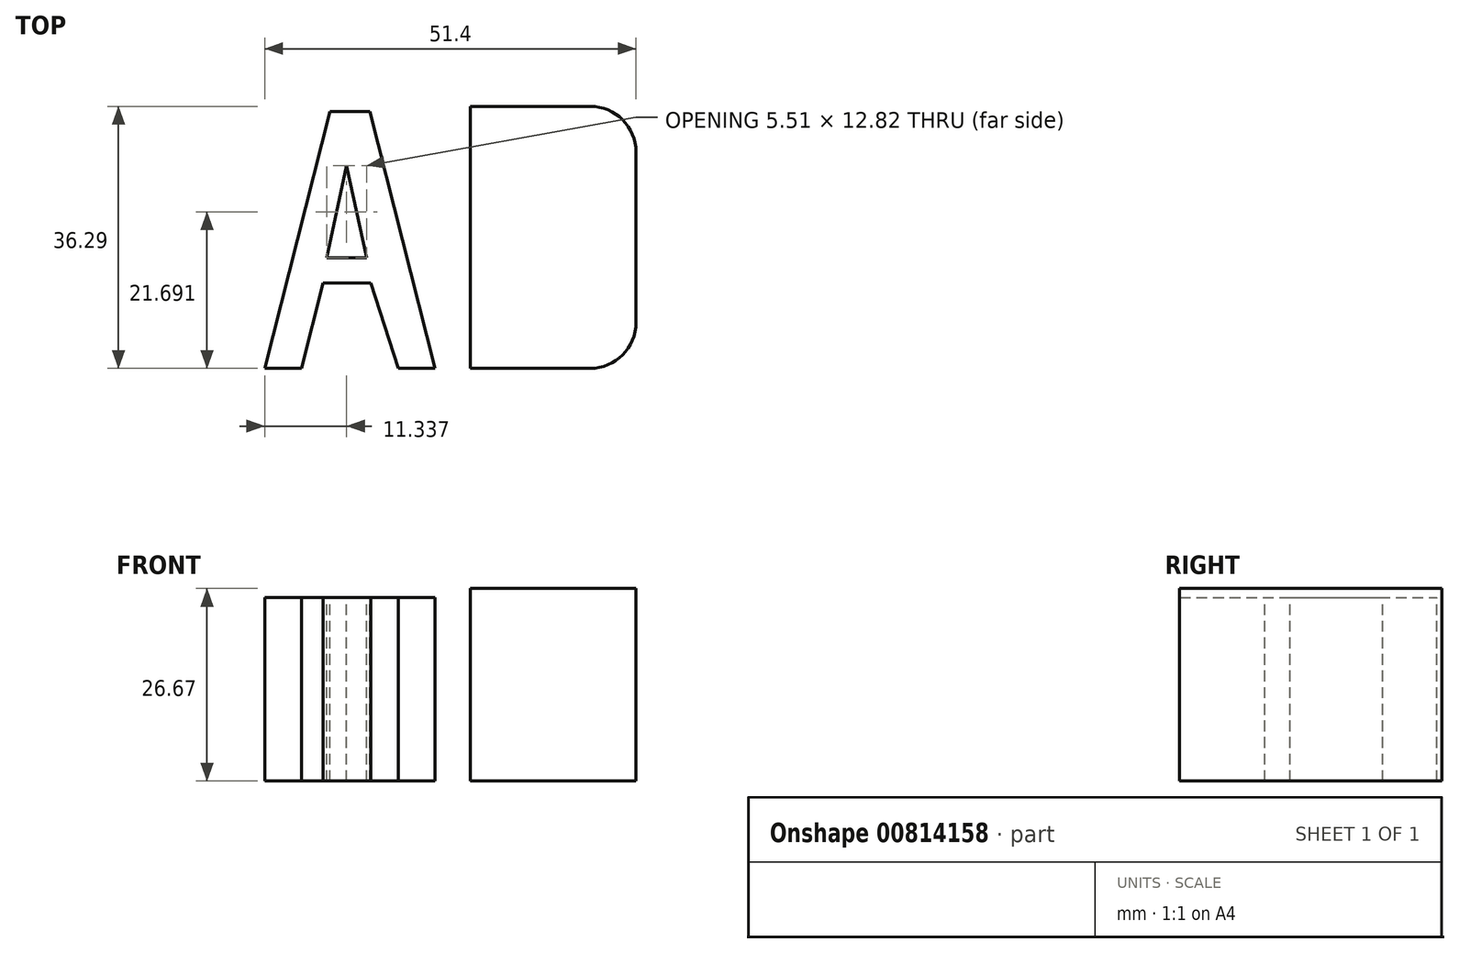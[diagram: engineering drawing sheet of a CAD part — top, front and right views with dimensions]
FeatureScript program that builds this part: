
annotation { "Feature Type Name" : "Feature", "Feature Type Description" : "" }
export const myFeature = defineFeature(function(context is Context, id is Id, definition is map)
    precondition{}
    {
        {
            var Q0;
            Q0=qCreatedBy(makeId("Top.planeOp"),FACE);
            var sketch = newSketch(context, id + "F0", { "sketchPlane" : qUnion([Q0])});
            skLineSegment(sketch, "E0.bottom", {"start": v(-107.36, 31.38) * mm, "end": v(-69.58, 31.38) * mm});
            skLineSegment(sketch, "E0.top", {"start": v(-107.36, -34.32) * mm, "end": v(-69.58, -34.32) * mm});
            skLineSegment(sketch, "E0.left", {"start": v(-107.36, 31.38) * mm, "end": v(-107.36, -34.32) * mm});
            skLineSegment(sketch, "E0.right", {"start": v(-69.58, 31.38) * mm, "end": v(-69.58, -34.32) * mm});
            skSolve(sketch);
        }
        {
            var Q0;
            Q0 = qSketchRegion(id + "F0", true);
            extrude(context, id + "F1", {"entities" : qUnion([Q0]), "depth" : 25.4 * mm, "offsetDistance" : 25.4 * mm});
        }
        {
            var Q0;
            Q0=makeQuery(id+"F1.opExtrude","CAP_FACE",FACE,{"disambiguationData":[OSD([sQuery(id+"F0.wireOp",EDGE,"E0.bottom"),sQuery(id+"F0.wireOp",EDGE,"E0.top"),sQuery(id+"F0.wireOp",EDGE,"E0.left"),sQuery(id+"F0.wireOp",EDGE,"E0.right")])],"isStart":false});
            var sketch = newSketch(context, id + "F2", { "sketchPlane" : qUnion([Q0])});
            skLineSegment(sketch, "E1", {"start": v(-96.38, -34.32) * mm, "end": v(-93.9, -22.41) * mm});
            skLineSegment(sketch, "E2", {"start": v(-93.9, -22.41) * mm, "end": v(-85.2, -22.41) * mm});
            skLineSegment(sketch, "E3", {"start": v(-85.2, -22.41) * mm, "end": v(-82.97, -34.32) * mm});
            skLineSegment(sketch, "E4", {"start": v(-82.97, -34.32) * mm, "end": v(-96.38, -34.32) * mm});
            skLineSegment(sketch, "E5", {"start": v(-77.89, -34.32) * mm, "end": v(-86.88, 1.24) * mm});
            skLineSegment(sketch, "E6", {"start": v(-86.88, 1.24) * mm, "end": v(-92.4, 1.24) * mm});
            skLineSegment(sketch, "E7", {"start": v(-92.4, 1.24) * mm, "end": v(-101.46, -34.32) * mm});
            skLineSegment(sketch, "E8", {"start": v(-101.46, -34.32) * mm, "end": v(-77.89, -34.32) * mm});
            skLineSegment(sketch, "E9", {"start": v(-89.64, -5.09) * mm, "end": v(-93.43, -19.95) * mm});
            skLineSegment(sketch, "E10", {"start": v(-93.43, -19.95) * mm, "end": v(-85.75, -19.95) * mm});
            skLineSegment(sketch, "E11", {"start": v(-89.64, -5.09) * mm, "end": v(-85.75, -19.95) * mm});
            skLineSegment(sketch, "E12", {"start": v(-82.97, -34.32) * mm, "end": v(-77.89, -34.32) * mm});
            skLineSegment(sketch, "E13", {"start": v(-96.38, -34.32) * mm, "end": v(-101.46, -34.32) * mm});
            skLineSegment(sketch, "E14", {"start": v(-77.89, -34.32) * mm, "end": v(-69.58, -34.32) * mm});
            skLineSegment(sketch, "E15", {"start": v(-69.58, -34.32) * mm, "end": v(-69.58, 31.38) * mm});
            skLineSegment(sketch, "E16", {"start": v(-69.58, 31.38) * mm, "end": v(-107.36, 31.38) * mm});
            skLineSegment(sketch, "E17", {"start": v(-107.36, 31.38) * mm, "end": v(-107.36, -34.32) * mm});
            skLineSegment(sketch, "E18", {"start": v(-107.36, -34.32) * mm, "end": v(-101.46, -34.32) * mm});
            skLineSegment(sketch, "E19", {"start": v(-101.46, -34.32) * mm, "end": v(-92.4, 1.24) * mm});
            skLineSegment(sketch, "E20", {"start": v(-92.4, 1.24) * mm, "end": v(-86.88, 1.24) * mm});
            skLineSegment(sketch, "E21", {"start": v(-86.88, 1.24) * mm, "end": v(-77.89, -34.32) * mm});
            skSolve(sketch);
        }
        {
            var Q0;
            Q0 = qSketchRegion(id + "F0", true);
            extrude(context, id + "F3", {"entities" : qUnion([Q0]), "operationType" : NewBodyOperationType.ADD, "depth" : 25.4 * mm, "offsetDistance" : 25.4 * mm});
        }
        {
            var Q0;
            Q0=makeQuery(id+"F2.imprint","IMPRINT",FACE,{"disambiguationData":[TD([[makeQuery(id+"F2.imprint","IMPRINT",EDGE,{"derivedFrom":sQuery(id+"F2.wireOp",EDGE,"E14")}),1.0]])]});
            extrude(context, id + "F4", {"entities" : qUnion([Q0]), "operationType" : NewBodyOperationType.REMOVE, "oppositeDirection" : true, "depth" : 25.4 * mm, "offsetDistance" : 25.4 * mm});
        }
        {
            var Q0;
            Q0=makeQuery(id+"F1.opExtrude","CAP_FACE",FACE,{"disambiguationData":[OSD([sQuery(id+"F0.wireOp",EDGE,"E0.bottom"),sQuery(id+"F0.wireOp",EDGE,"E0.top"),sQuery(id+"F0.wireOp",EDGE,"E0.left"),sQuery(id+"F0.wireOp",EDGE,"E0.right")])],"isStart":false});
            var sketch = newSketch(context, id + "F5", { "sketchPlane" : qUnion([Q0])});
            skLineSegment(sketch, "E22", {"start": v(-96.38, -34.32) * mm, "end": v(-93.38, -22.52) * mm});
            skLineSegment(sketch, "E23", {"start": v(-93.38, -22.52) * mm, "end": v(-86.76, -22.52) * mm});
            skLineSegment(sketch, "E24", {"start": v(-86.76, -22.52) * mm, "end": v(-82.97, -34.32) * mm});
            skLineSegment(sketch, "E25", {"start": v(-82.97, -34.32) * mm, "end": v(-77.89, -34.32) * mm});
            skLineSegment(sketch, "E26", {"start": v(-96.38, -34.32) * mm, "end": v(-101.46, -34.32) * mm});
            skLineSegment(sketch, "E27", {"start": v(-90.15, -6.23) * mm, "end": v(-92.88, -19.05) * mm});
            skLineSegment(sketch, "E28", {"start": v(-92.88, -19.05) * mm, "end": v(-87.37, -19.05) * mm});
            skLineSegment(sketch, "E29", {"start": v(-87.37, -19.05) * mm, "end": v(-90.15, -6.23) * mm});
            skSolve(sketch);
        }
        {
            var Q0;
            Q0=makeQuery(id+"F5.imprint","IMPRINT",FACE,{"disambiguationData":[TD([[makeQuery(id+"F5.imprint","IMPRINT",EDGE,{"derivedFrom":sQuery(id+"F5.wireOp",EDGE,"E27")}),1.0]])]});
            var Q1;
            {var subQ0=sQuery(id+"F5.wireOp",EDGE,"E22");Q1=makeQuery(id+"F5.imprint","IMPRINT",FACE,{"disambiguationData":[TD([[makeQuery(id+"F5.imprint","IMPRINT",EDGE,{"derivedFrom":subQ0}),-1.0]])]});}
            extrude(context, id + "F6", {"entities" : qUnion([Q0, Q1]), "operationType" : NewBodyOperationType.REMOVE, "oppositeDirection" : true, "depth" : 25.4 * mm, "offsetDistance" : 25.4 * mm});
        }
        {
            var Q0;
            Q0=qCreatedBy(makeId("Top.planeOp"),FACE);
            var sketch = newSketch(context, id + "F7", { "sketchPlane" : qUnion([Q0])});
            skLineSegment(sketch, "E30.bottom", {"start": v(-73, 1.96) * mm, "end": v(-56.4, 1.96) * mm});
            skLineSegment(sketch, "E30.top", {"start": v(-73, -34.33) * mm, "end": v(-56.4, -34.33) * mm});
            skLineSegment(sketch, "E30.left", {"start": v(-73, 1.96) * mm, "end": v(-73, -34.33) * mm});
            skLineSegment(sketch, "E30.right", {"start": v(-50.06, -4.39) * mm, "end": v(-50.06, -27.98) * mm});
            skPoint(sketch, "E31.visualSharp", {"position": v(-50.06, -34.33) * mm});
            skArc(sketch, "E31.filletArc", {"start": v(-56.4, -34.33) * mm, "mid": v(-51.92, -32.47) * mm, "end": v(-50.06, -27.98) * mm});
            skPoint(sketch, "E32.visualSharp", {"position": v(-50.06, 1.96) * mm});
            skArc(sketch, "E32.filletArc", {"start": v(-50.06, -4.39) * mm, "mid": v(-51.92, 0.1) * mm, "end": v(-56.4, 1.96) * mm});
            skSolve(sketch);
        }
        {
            var Q0;
            Q0 = qSketchRegion(id + "F7", true);
            extrude(context, id + "F8", {"entities" : qUnion([Q0]), "depth" : 26.67 * mm, "offsetDistance" : 25.4 * mm});
        }
    });
